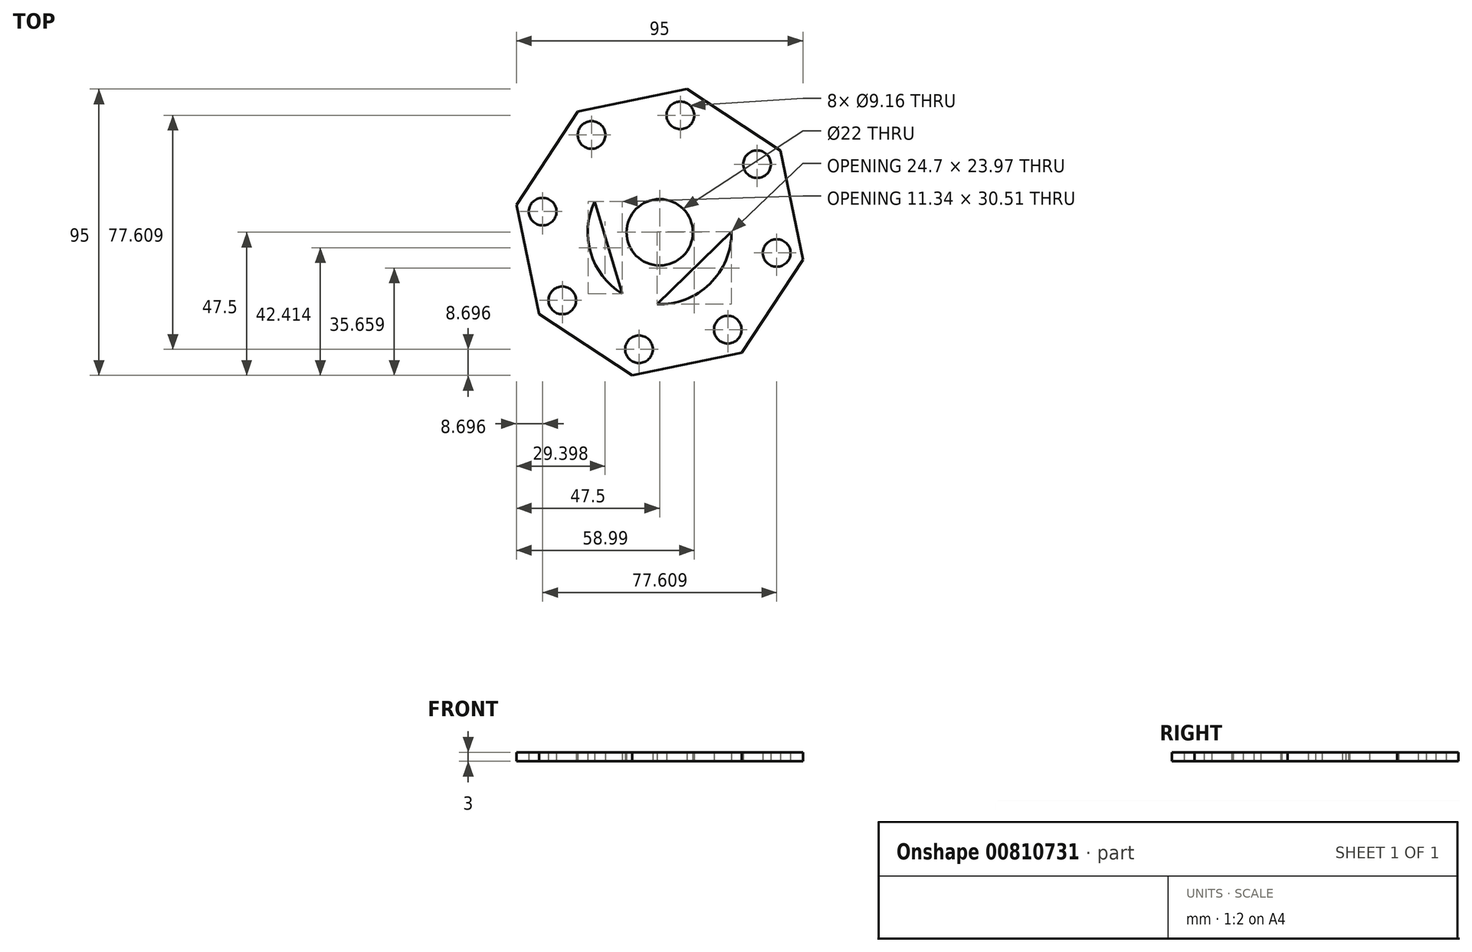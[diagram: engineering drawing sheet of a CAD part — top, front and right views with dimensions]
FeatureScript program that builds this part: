
annotation { "Feature Type Name" : "Feature", "Feature Type Description" : "" }
export const myFeature = defineFeature(function(context is Context, id is Id, definition is map)
    precondition{}
    {
        {
            var Q0;
            Q0=qCreatedBy(makeId("Top.planeOp"),FACE);
            var sketch = newSketch(context, id + "F0", { "sketchPlane" : qUnion([Q0])});
            skCircle(sketch, "E0", {"center": v(0, 0) * mm, "radius": 11 * mm});
            skSolve(sketch);
        }
        {
            var Q0;
            Q0 = qSketchRegion(id + "F0", true);
            var sketch = newSketch(context, id + "F1", { "sketchPlane" : qUnion([Q0])});
            skLineSegment(sketch, "E1.7", {"start": v(9.07, 47.5) * mm, "end": v(24.54, 37.34) * mm});
            skPoint(sketch, "E1.0.midPoint", {"position": v(43.75, 9.05) * mm});
            skCircle(sketch, "E2", {"center": v(6.86, 38.8) * mm, "radius": 4.58 * mm});
            skPoint(sketch, "E3.orphan", {"position": v(-27.17, 40) * mm});
            skPoint(sketch, "E4.orphan", {"position": v(-40, -27.17) * mm});
            skPoint(sketch, "E1.0.start.orphan", {"position": v(40, 27.17) * mm});
            skPoint(sketch, "E1.1.start.orphan", {"position": v(47.5, -9.07) * mm});
            skPoint(sketch, "E1.3.start.orphan", {"position": v(-9.07, -47.5) * mm});
            skLineSegment(sketch, "E5", {"start": v(9.07, 47.5) * mm, "end": v(-9.05, 43.75) * mm});
            skCircle(sketch, "E6.1.0", {"center": v(-22.59, 32.29) * mm, "radius": 4.58 * mm});
            skLineSegment(sketch, "E6.1.1", {"start": v(-27.17, 40) * mm, "end": v(-37.34, 24.54) * mm});
            skLineSegment(sketch, "E6.1.2", {"start": v(-27.17, 40) * mm, "end": v(-9.05, 43.75) * mm});
            skCircle(sketch, "E6.2.0", {"center": v(-38.8, 6.86) * mm, "radius": 4.58 * mm});
            skLineSegment(sketch, "E6.2.1", {"start": v(-47.5, 9.07) * mm, "end": v(-43.75, -9.05) * mm});
            skLineSegment(sketch, "E6.2.2", {"start": v(-47.5, 9.07) * mm, "end": v(-37.34, 24.54) * mm});
            skCircle(sketch, "E6.3.0", {"center": v(-32.29, -22.59) * mm, "radius": 4.58 * mm});
            skLineSegment(sketch, "E6.3.1", {"start": v(-40, -27.17) * mm, "end": v(-24.54, -37.34) * mm});
            skLineSegment(sketch, "E6.3.2", {"start": v(-40, -27.17) * mm, "end": v(-43.75, -9.05) * mm});
            skCircle(sketch, "E6.4.0", {"center": v(-6.86, -38.8) * mm, "radius": 4.58 * mm});
            skLineSegment(sketch, "E6.4.1", {"start": v(-9.07, -47.5) * mm, "end": v(9.05, -43.75) * mm});
            skLineSegment(sketch, "E6.4.2", {"start": v(-9.07, -47.5) * mm, "end": v(-24.54, -37.34) * mm});
            skCircle(sketch, "E6.5.0", {"center": v(22.59, -32.29) * mm, "radius": 4.58 * mm});
            skLineSegment(sketch, "E6.5.1", {"start": v(27.17, -40) * mm, "end": v(37.34, -24.54) * mm});
            skLineSegment(sketch, "E6.5.2", {"start": v(27.17, -40) * mm, "end": v(9.05, -43.75) * mm});
            skCircle(sketch, "E6.6.0", {"center": v(38.8, -6.86) * mm, "radius": 4.58 * mm});
            skLineSegment(sketch, "E6.6.1", {"start": v(47.5, -9.07) * mm, "end": v(43.75, 9.05) * mm});
            skLineSegment(sketch, "E6.6.2", {"start": v(47.5, -9.07) * mm, "end": v(37.34, -24.54) * mm});
            skCircle(sketch, "E6.7.0", {"center": v(32.29, 22.59) * mm, "radius": 4.58 * mm});
            skLineSegment(sketch, "E6.7.1", {"start": v(40, 27.17) * mm, "end": v(24.54, 37.34) * mm});
            skLineSegment(sketch, "E6.7.2", {"start": v(40, 27.17) * mm, "end": v(43.75, 9.05) * mm});
            skPoint(sketch, "E6.center", {"position": v(0, 0) * mm});
            skArc(sketch, "E7", {"start": v(21.36, 10.58) * mm, "mid": v(5.5, 23.2) * mm, "end": v(-14.33, 19.05) * mm});
            skPoint(sketch, "E8.8.end.orphan", {"position": v(23.84, 0) * mm});
            skLineSegment(sketch, "E9", {"start": v(-21.56, 10.17) * mm, "end": v(-12.43, -20.34) * mm});
            skLineSegment(sketch, "E10", {"start": v(-12.43, -20.34) * mm, "end": v(-21.56, 10.17) * mm});
            skLineSegment(sketch, "E11", {"start": v(21.36, 10.58) * mm, "end": v(-14.33, 19.05) * mm});
            skLineSegment(sketch, "E12", {"start": v(23.84, 0.14) * mm, "end": v(-0.86, -23.82) * mm});
            skArc(sketch, "E13.trimOffspring", {"start": v(-0.86, -23.82) * mm, "mid": v(16.6, -17.1) * mm, "end": v(23.84, 0.14) * mm, "construction": true});
            skArc(sketch, "E14.trimOffspring", {"start": v(-21.56, 10.17) * mm, "mid": v(-22.84, -6.83) * mm, "end": v(-12.43, -20.34) * mm});
            skArc(sketch, "E15.trimOffspring", {"start": v(-0.86, -23.82) * mm, "mid": v(16.6, -17.1) * mm, "end": v(23.84, 0.14) * mm});
            skArc(sketch, "E16.trimOffspring", {"start": v(21.36, 10.58) * mm, "mid": v(5.5, 23.2) * mm, "end": v(-14.33, 19.05) * mm, "construction": true});
            skCircle(sketch, "E17", {"center": v(0, 0) * mm, "radius": 11 * mm});
            skSolve(sketch);
        }
        {
            var Q0;
            Q0 = qSketchRegion(id + "F1", true);
            var Q1;
            Q1=makeQuery(id+"F1.imprint","IMPRINT",FACE,{"disambiguationData":[TD([[makeQuery(id+"F1.imprint","IMPRINT",EDGE,{"derivedFrom":sQuery(id+"F1.wireOp",EDGE,"E7")}),1.0]])]});
            var Q2;
            {var subQ0=sQuery(id+"F1.wireOp",EDGE,"E8.6");Q2=makeQuery(id+"F1.imprint","IMPRINT",FACE,{"disambiguationData":[TD([[makeQuery(id+"F1.imprint","IMPRINT",EDGE,{"derivedFrom":subQ0}),1.0]])]});}
            var Q3;
            Q3=makeQuery(id+"F1.imprint","IMPRINT",FACE,{"disambiguationData":[TD([[makeQuery(id+"F1.imprint","IMPRINT",EDGE,{"derivedFrom":sQuery(id+"F1.wireOp",EDGE,"E8.0")}),-1.0]])]});
            var Q4;
            Q4=makeQuery(id+"F1.imprint","IMPRINT",FACE,{"disambiguationData":[TD([[makeQuery(id+"F1.imprint","IMPRINT",EDGE,{"derivedFrom":sQuery(id+"F1.wireOp",EDGE,"c2d0e386-0c78-4903-a071-65d3bd791b67.0")}),-1.0]])]});
            var Q5;
            Q5=makeQuery(id+"F0.imprint","IMPRINT",FACE,{"disambiguationData":[TD([[makeQuery(id+"F0.imprint","IMPRINT",EDGE,{"derivedFrom":sQuery(id+"F0.wireOp",EDGE,"E0")}),-1.0]])]});
            var Q6;
            {var subQ0=sQuery(id+"F1.wireOp",EDGE,"E8.4");Q6=makeQuery(id+"F1.imprint","IMPRINT",FACE,{"disambiguationData":[TD([[makeQuery(id+"F1.imprint","IMPRINT",EDGE,{"derivedFrom":subQ0}),1.0]])]});}
            var Q7;
            {var subQ0=sQuery(id+"F1.wireOp",EDGE,"E8.5");Q7=makeQuery(id+"F1.imprint","IMPRINT",FACE,{"disambiguationData":[TD([[makeQuery(id+"F1.imprint","IMPRINT",EDGE,{"derivedFrom":subQ0}),1.0]])]});}
            extrude(context, id + "F2", {"entities" : qUnion([Q0, Q1, Q2, Q3, Q4, Q5, Q6, Q7]), "depth" : 3 * mm, "offsetDistance" : 25 * mm});
        }
    });
